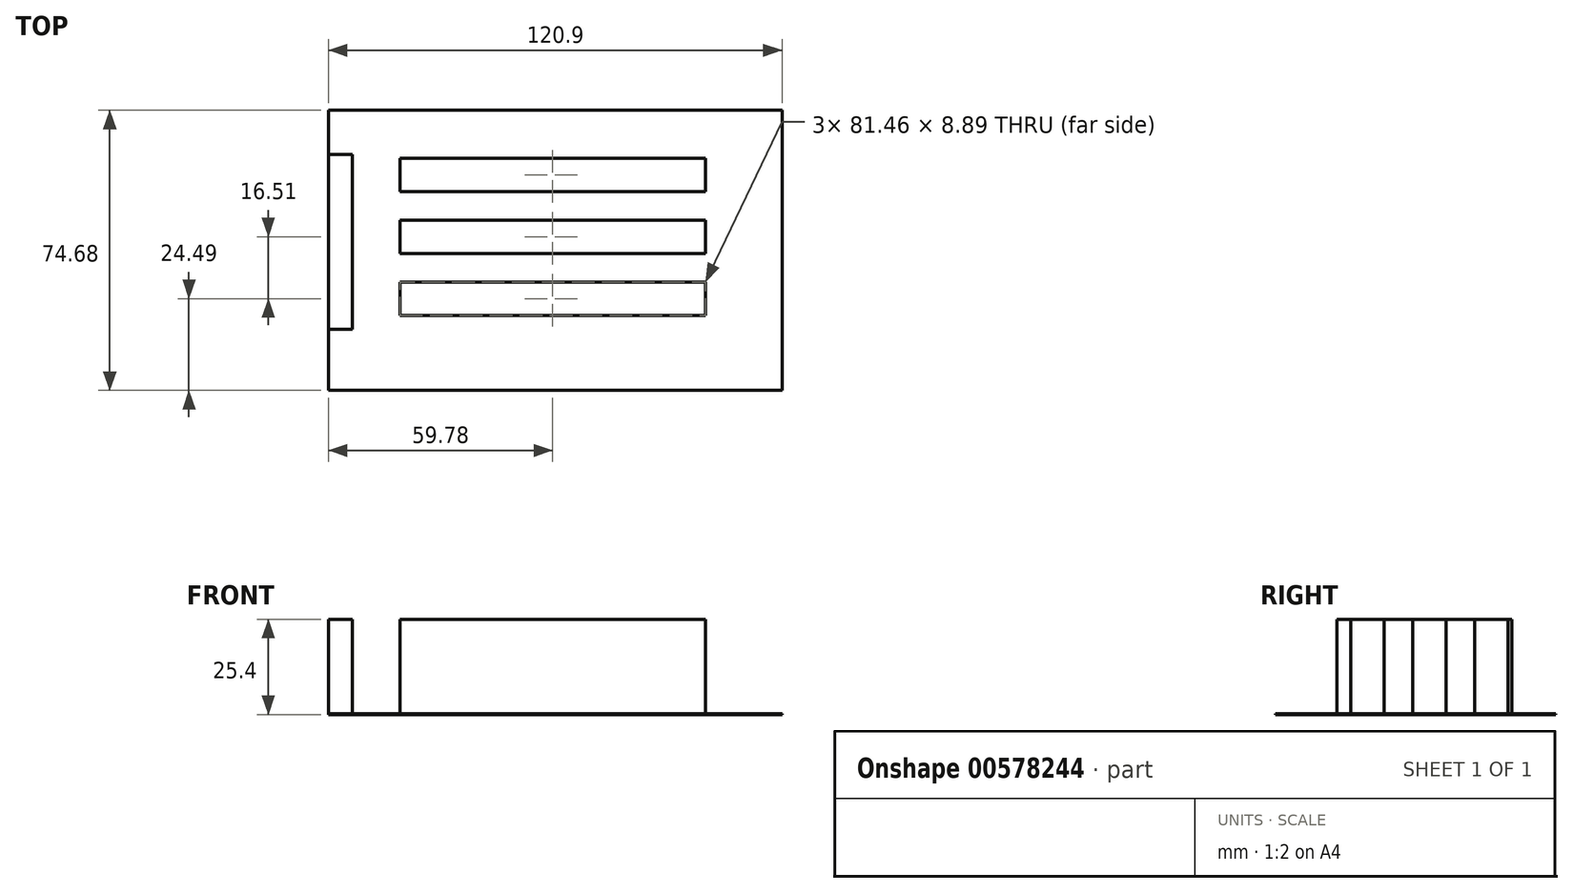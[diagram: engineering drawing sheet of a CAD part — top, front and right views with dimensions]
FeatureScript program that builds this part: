
annotation { "Feature Type Name" : "Feature", "Feature Type Description" : "" }
export const myFeature = defineFeature(function(context is Context, id is Id, definition is map)
    precondition{}
    {
        {
            var Q0;
            Q0=qCreatedBy(makeId("Top.planeOp"),FACE);
            var sketch = newSketch(context, id + "F0", { "sketchPlane" : qUnion([Q0])});
            skLineSegment(sketch, "E0.bottom", {"start": v(60.45, 37.34) * mm, "end": v(-60.45, 37.34) * mm});
            skLineSegment(sketch, "E0.top", {"start": v(60.45, -37.34) * mm, "end": v(-60.45, -37.34) * mm});
            skLineSegment(sketch, "E0.left", {"start": v(60.45, 37.34) * mm, "end": v(60.45, -37.34) * mm});
            skLineSegment(sketch, "E0.right", {"start": v(-60.45, 37.34) * mm, "end": v(-60.45, -37.34) * mm});
            skPoint(sketch, "E0.middle", {"position": v(0, 0) * mm});
            skLineSegment(sketch, "E1.bottom", {"start": v(-41.4, 24.61) * mm, "end": v(40.06, 24.61) * mm});
            skLineSegment(sketch, "E1.top", {"start": v(-41.4, 15.72) * mm, "end": v(40.06, 15.72) * mm});
            skLineSegment(sketch, "E1.left", {"start": v(-41.4, 24.61) * mm, "end": v(-41.4, 15.72) * mm});
            skLineSegment(sketch, "E1.right", {"start": v(40.06, 24.61) * mm, "end": v(40.06, 15.72) * mm});
            skLineSegment(sketch, "E2.bottom", {"start": v(40.06, -0.79) * mm, "end": v(-41.4, -0.79) * mm});
            skLineSegment(sketch, "E2.top", {"start": v(40.06, 8.1) * mm, "end": v(-41.4, 8.1) * mm});
            skLineSegment(sketch, "E2.left", {"start": v(40.06, -0.79) * mm, "end": v(40.06, 8.1) * mm});
            skLineSegment(sketch, "E2.right", {"start": v(-41.4, -0.79) * mm, "end": v(-41.4, 8.1) * mm});
            skLineSegment(sketch, "E3.bottom", {"start": v(-41.4, -8.4) * mm, "end": v(40.06, -8.4) * mm});
            skLineSegment(sketch, "E3.top", {"start": v(-41.4, -17.3) * mm, "end": v(40.06, -17.3) * mm});
            skLineSegment(sketch, "E3.left", {"start": v(-41.4, -8.4) * mm, "end": v(-41.4, -17.3) * mm});
            skLineSegment(sketch, "E3.right", {"start": v(40.06, -8.4) * mm, "end": v(40.06, -17.3) * mm});
            skLineSegment(sketch, "E4.bottom", {"start": v(-60.45, 25.54) * mm, "end": v(-54.1, 25.54) * mm});
            skLineSegment(sketch, "E4.top", {"start": v(-60.45, -21.01) * mm, "end": v(-54.1, -21.01) * mm});
            skLineSegment(sketch, "E4.left", {"start": v(-60.45, 25.54) * mm, "end": v(-60.45, -21.01) * mm});
            skLineSegment(sketch, "E4.right", {"start": v(-54.1, 25.54) * mm, "end": v(-54.1, -21.01) * mm});
            skSolve(sketch);
        }
        {
            var Q0;
            Q0=makeQuery(id+"F0.imprint","IMPRINT",FACE,{"disambiguationData":[TD([[makeQuery(id+"F0.imprint","IMPRINT",EDGE,{"derivedFrom":sQuery(id+"F0.wireOp",EDGE,"E1.bottom")}),-1.0]])]});
            var Q1;
            Q1=makeQuery(id+"F0.imprint","IMPRINT",FACE,{"disambiguationData":[TD([[makeQuery(id+"F0.imprint","IMPRINT",EDGE,{"derivedFrom":sQuery(id+"F0.wireOp",EDGE,"E4.bottom")}),-1.0]])]});
            var Q2;
            Q2=makeQuery(id+"F0.imprint","IMPRINT",FACE,{"disambiguationData":[TD([[makeQuery(id+"F0.imprint","IMPRINT",EDGE,{"derivedFrom":sQuery(id+"F0.wireOp",EDGE,"E2.bottom")}),-1.0]])]});
            var Q3;
            Q3=makeQuery(id+"F0.imprint","IMPRINT",FACE,{"disambiguationData":[TD([[makeQuery(id+"F0.imprint","IMPRINT",EDGE,{"derivedFrom":sQuery(id+"F0.wireOp",EDGE,"E3.bottom")}),-1.0]])]});
            extrude(context, id + "F1", {"entities" : qUnion([Q0, Q1, Q2, Q3]), "depth" : 25.4 * mm, "offsetDistance" : 25.4 * mm});
        }
        {
            var Q0;
            {var subQ4=sQuery(id+"F0.wireOp",EDGE,"E0.bottom");Q0=makeQuery(id+"F0.imprint","IMPRINT",FACE,{"disambiguationData":[TD([[makeQuery(id+"F0.imprint","IMPRINT",EDGE,{"derivedFrom":subQ4}),1.0]])]});}
            extrude(context, id + "F2", {"entities" : qUnion([Q0]), "depth" : 0.25 * mm, "offsetDistance" : 25.4 * mm});
        }
    });
